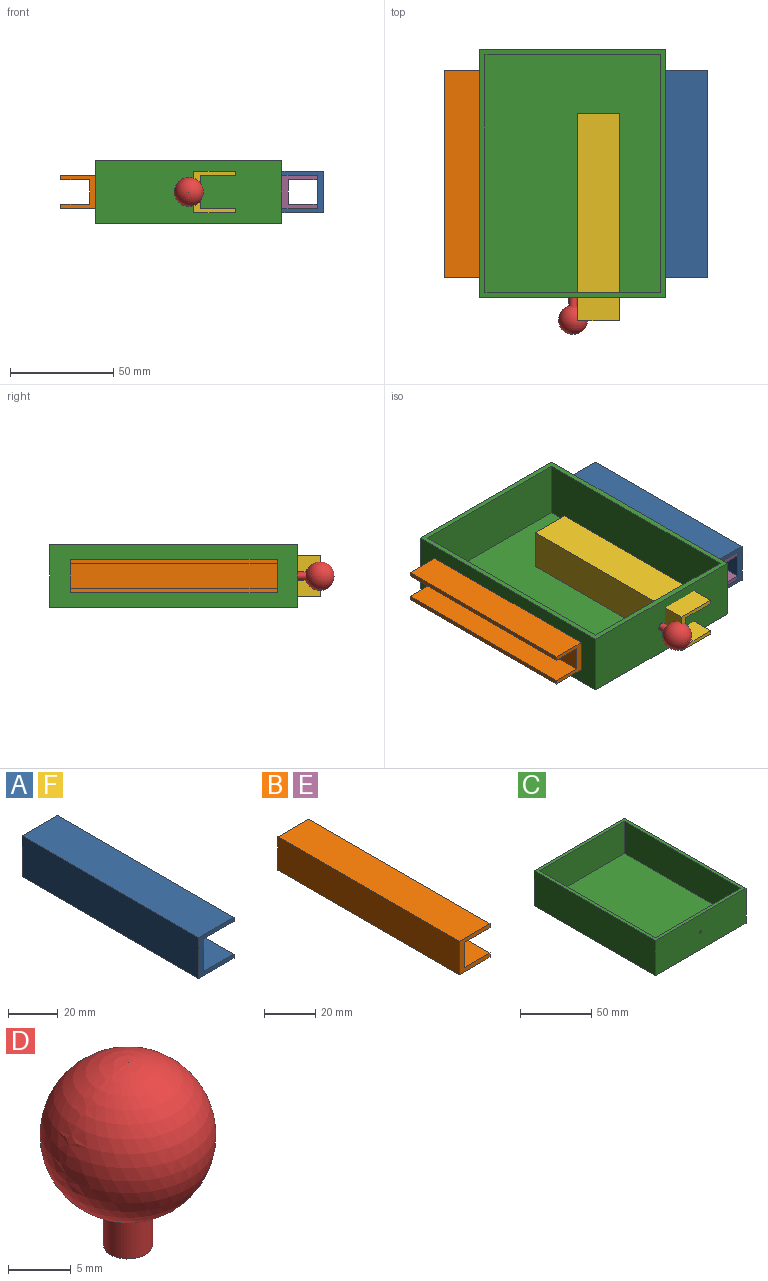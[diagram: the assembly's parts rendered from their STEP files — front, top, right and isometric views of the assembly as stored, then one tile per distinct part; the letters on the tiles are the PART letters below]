
ASSEMBLY  parts=6 mates=5
PART A: 10 faces, bbox 20x100x20 mm
  f0: plane 100x20mm, normal (0,0,-1), area 2000mm2, adj f1,f7,f8,f9
  f1: plane 100x2mm, normal (1,0,0), area 200mm2, adj f0,f2,f8,f9
  f2: plane 100x17mm, normal (0,0,1), area 1700mm2, adj f1,f3,f8,f9
  f3: plane 100x16mm, normal (1,0,0), area 1600mm2, adj f2,f4,f8,f9
  f4: plane 100x17mm, normal (0,0,-1), area 1700mm2, adj f3,f5,f8,f9
  f5: plane 100x2mm, normal (1,0,0), area 200mm2, adj f4,f6,f8,f9
  f6: plane 100x20mm, normal (0,0,1), area 2000mm2, adj f5,f7,f8,f9
  f7: plane 100x20mm, normal (-1,0,0), area 2000mm2, adj f0,f6,f8,f9
  f8: plane 20x20mm, normal (0,-1,0), area 128mm2, adj f0,f1,f2,f3,f4,f5,f6,f7
  f9: plane 20x20mm, normal (0,1,0), area 128mm2, adj f0,f1,f2,f3,f4,f5,f6,f7
PART B: 10 faces, bbox 17x100x16 mm
  f0: plane 100x17mm, normal (0,0,-1), area 1700mm2, adj f1,f7,f8,f9
  f1: plane 100x2mm, normal (1,0,0), area 200mm2, adj f0,f2,f8,f9
  f2: plane 100x14mm, normal (0,0,1), area 1400mm2, adj f1,f3,f8,f9
  f3: plane 100x12mm, normal (1,0,0), area 1200mm2, adj f2,f4,f8,f9
  f4: plane 100x14mm, normal (0,0,-1), area 1400mm2, adj f3,f5,f8,f9
  f5: plane 100x2mm, normal (1,0,0), area 200mm2, adj f4,f6,f8,f9
  f6: plane 100x17mm, normal (0,0,1), area 1700mm2, adj f5,f7,f8,f9
  f7: plane 100x16mm, normal (-1,0,0), area 1600mm2, adj f0,f6,f8,f9
  f8: plane 17x16mm, normal (0,-1,0), area 104mm2, adj f0,f1,f2,f3,f4,f5,f6,f7
  f9: plane 17x16mm, normal (0,1,0), area 104mm2, adj f0,f1,f2,f3,f4,f5,f6,f7
PART C: 12 faces, bbox 90x120x30 mm
  f0: plane 120x90mm, normal (0,0,1), area 1025mm2, adj f1,f2,f3,f4,f6,f7,f8,f9
  f1: plane 90x30mm, normal (0,-1,0), area 2696.9mm2, adj f0,f2,f4,f5,f11
  f2: plane 120x30mm, normal (1,0,0), area 3600mm2, adj f0,f1,f3,f5
  f3: plane 90x30mm, normal (0,1,0), area 2700mm2, adj f0,f2,f4,f5
  f4: plane 120x30mm, normal (-1,0,0), area 3600mm2, adj f0,f1,f3,f5
  f5: plane 120x90mm, normal (0,0,-1), area 10800mm2, adj f1,f2,f3,f4
  f6: plane 85x27.5mm, normal (0,1,0), area 2334.4mm2, adj f0,f7,f9,f10,f11
  f7: plane 115x27.5mm, normal (-1,0,0), area 3162.5mm2, adj f0,f6,f8,f10
  f8: plane 85x27.5mm, normal (0,-1,0), area 2337.5mm2, adj f0,f7,f9,f10
  f9: plane 115x27.5mm, normal (1,0,0), area 3162.5mm2, adj f0,f6,f8,f10
  f10: plane 115x85mm, normal (0,0,1), area 9775mm2, adj f6,f7,f8,f9
  f11: cylinder r=1mm len=2.5mm, axis (0,-1,0), area 15.7mm2, adj f1,f6
PART D: 3 faces, bbox 14x14x17.7 mm
  f0: plane 3.92x3.92mm, normal (0,0,-1), area 12.1mm2, adj f2
  f1: sphere r=7mm, area 603.4mm2, adj f2
  f2: cylinder r=1.96mm len=3.98mm, axis (0,0,-1), area 49mm2, adj f0,f1
PART E: same geometry as B
PART F: same geometry as A
PLACE A rot(axis=(0,-1,0),180deg) t=(149.52,6.62,-9.73)mm
PLACE B rot(axis=(0,1,0),180deg) t=(41.02,6.62,-9.73)mm
PLACE C t=(94.52,-43.38,-24.73)mm
PLACE D rot(axis=(1,0,0),90deg) t=(94.52,-114.08,-9.73)mm
PLACE E t=(148.02,6.62,-9.73)mm
PLACE F t=(106.92,-14.5,-9.73)mm fixed
MATE planar E.f6 <-> A.f2  axis (0,0,1) through (148.02,-43.38,-1.73)mm
MATE fastened E.f7 <-> C.f2  axis (-1,0,0) through (139.52,-43.38,-9.73)mm
MATE planar B.f0 <-> F.f4  axis (0,0,1) through (41.02,-43.38,-1.73)mm
MATE fastened B.f7 <-> C.f4  axis (1,0,0) through (49.52,-43.38,-9.73)mm
MATE fastened D.f2 <-> C.f11  axis (0,1,0) through (94.52,-103.38,-9.73)mm
